# Revit family: LBSLEDA
name_source: partatom
category: Lighting Fixtures
revit_build: Autodesk Revit Architecture 2012 (Build: 20110309_2315(x64)
units: mm (PartAtom-declared; Revit-internal decimal feet)

## types (1)
- LBSLEDA10L30K9 WH
    Apparent Load = 0 VA
    Backbox = White
    CRI = 90+ CRI
    Color Filter = 16777215
    Default Elevation = 4' - 0"
    Description = Designed for use in new construction or retrofit IC or Non-IC applications
    Dimming Lamp Color Temperature Shift = <None>
    Glass = White Glass
    Lamp = LED Lamp
    Manufacturer = Prescolite Lighting
    Manufacturer Fax = (866)-898-0131
    Model = LBSLEDA
    Photometric Web File = LBSLEDA10L30K9 WH.ies
    Product Documentation Link = http://www.prescolite.com
    Product Page URL = http://www.prescolite.com
    Tilt Angle = -90.00°
    URL = http://www.prescolite.com
    Voltage = 120 V
    Watts = 17 W

## geometry (parser evidence)
native form markers: Sweep x1
no freeform markers — native parametric forms only
